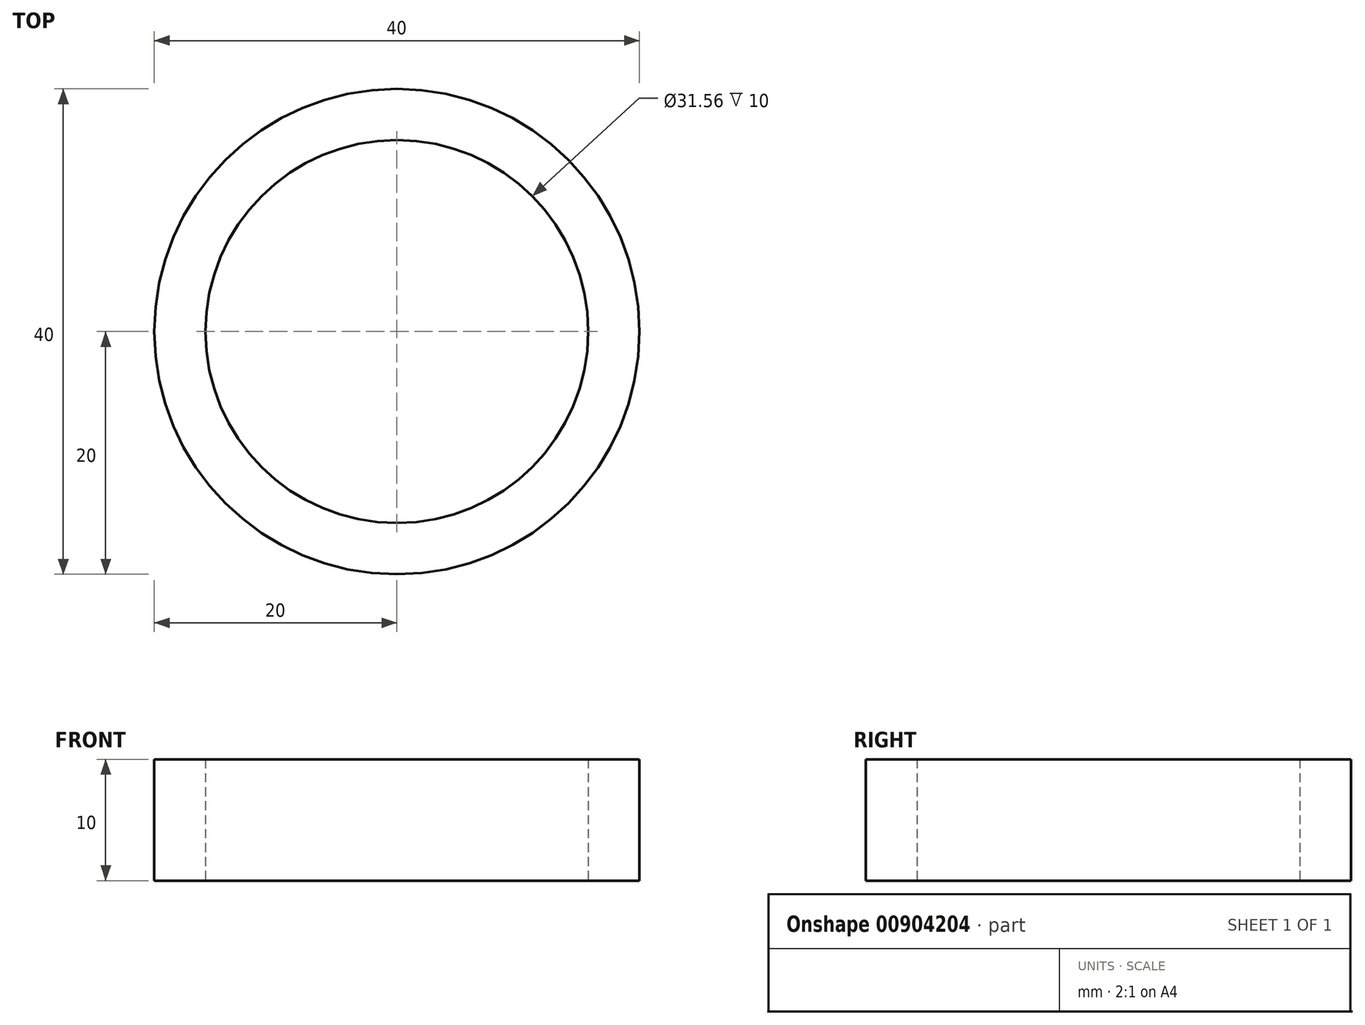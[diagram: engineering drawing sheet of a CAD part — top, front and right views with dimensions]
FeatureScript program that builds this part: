
annotation { "Feature Type Name" : "Feature", "Feature Type Description" : "" }
export const myFeature = defineFeature(function(context is Context, id is Id, definition is map)
    precondition{}
    {
        {
            var Q0;
            Q0=qCreatedBy(makeId("Top.planeOp"),FACE);
            var sketch = newSketch(context, id + "F0", { "sketchPlane" : qUnion([Q0])});
            skCircle(sketch, "E0.cCircle", {"center": v(0, 0) * mm, "radius": 14.22 * mm, "construction": true});
            skLineSegment(sketch, "E0.0", {"start": v(15.39, -3.51) * mm, "end": v(6.85, -14.22) * mm});
            skLineSegment(sketch, "E0.1", {"start": v(6.85, -14.22) * mm, "end": v(-6.85, -14.22) * mm});
            skLineSegment(sketch, "E0.2", {"start": v(-6.85, -14.22) * mm, "end": v(-15.39, -3.51) * mm});
            skLineSegment(sketch, "E0.3", {"start": v(-15.39, -3.51) * mm, "end": v(-12.34, 9.84) * mm});
            skLineSegment(sketch, "E0.4", {"start": v(-12.34, 9.84) * mm, "end": v(0, 15.78) * mm});
            skLineSegment(sketch, "E0.5", {"start": v(0, 15.78) * mm, "end": v(12.34, 9.84) * mm});
            skLineSegment(sketch, "E0.6", {"start": v(12.34, 9.84) * mm, "end": v(15.39, -3.51) * mm});
            skPoint(sketch, "E0.0.midPoint", {"position": v(11.12, -8.87) * mm});
            skCircle(sketch, "E1", {"center": v(0, 0) * mm, "radius": 20 * mm});
            skCircle(sketch, "E2", {"center": v(0, 0) * mm, "radius": 15.78 * mm});
            skSolve(sketch);
        }
        {
            var Q0;
            Q0=makeQuery(id+"F0.imprint","IMPRINT",FACE,{"disambiguationData":[TD([[makeQuery(id+"F0.imprint","IMPRINT",EDGE,{"derivedFrom":sQuery(id+"F0.wireOp",EDGE,"E1")}),1.0]])]});
            extrude(context, id + "F1", {"entities" : qUnion([Q0]), "depth" : 10 * mm, "offsetDistance" : 25 * mm});
        }
    });
